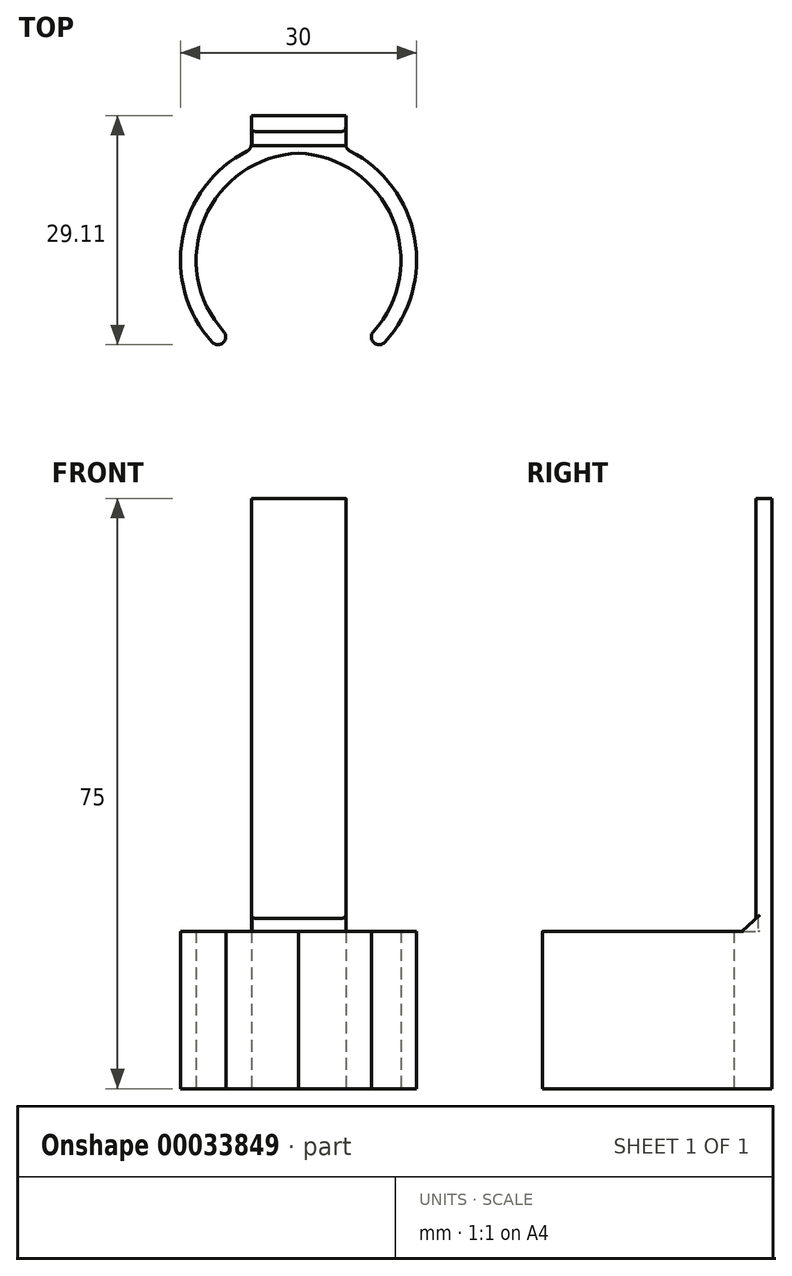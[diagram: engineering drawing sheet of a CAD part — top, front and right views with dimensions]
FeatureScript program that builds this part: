
annotation { "Feature Type Name" : "Feature", "Feature Type Description" : "" }
export const myFeature = defineFeature(function(context is Context, id is Id, definition is map)
    precondition{}
    {
        {
            var Q0;
            Q0=qCreatedBy(makeId("Top.planeOp"),FACE);
            var sketch = newSketch(context, id + "F0", { "sketchPlane" : qUnion([Q0])});
            skCircle(sketch, "E0", {"center": v(0, 0) * mm, "radius": 14.5 * mm, "construction": true});
            skCircle(sketch, "E1", {"center": v(0, 0) * mm, "radius": 12.5 * mm, "construction": true});
            skLineSegment(sketch, "E2", {"start": v(0, 0) * mm, "end": v(10.25, -10.25) * mm, "construction": true});
            skArc(sketch, "E3", {"start": v(9.5, -8.16) * mm, "mid": v(11.95, 6.19) * mm, "end": v(0, 14.5) * mm});
            skArc(sketch, "E4.0", {"start": v(10.98, -9.5) * mm, "mid": v(14.75, 3.74) * mm, "end": v(6.54, 14.8) * mm});
            skLineSegment(sketch, "E5", {"start": v(9.53, -9.53) * mm, "end": v(9.53, -9.53) * mm});
            skPoint(sketch, "E6.visualSharp", {"position": v(8.84, -8.84) * mm});
            skArc(sketch, "E6.filletArc", {"start": v(9.5, -8.16) * mm, "mid": v(9.24, -8.85) * mm, "end": v(9.53, -9.53) * mm});
            skPoint(sketch, "E7.visualSharp", {"position": v(10.25, -10.25) * mm});
            skArc(sketch, "E7.filletArc", {"start": v(9.53, -9.53) * mm, "mid": v(10.27, -9.83) * mm, "end": v(10.98, -9.5) * mm});
            skArc(sketch, "E8.MirrorCS", {"start": v(-10.98, -9.5) * mm, "mid": v(-14.75, 3.74) * mm, "end": v(-6.54, 14.8) * mm});
            skArc(sketch, "E9.MirrorCS", {"start": v(-9.5, -8.16) * mm, "mid": v(-11.95, 6.19) * mm, "end": v(0, 14.5) * mm});
            skArc(sketch, "E10.MirrorCS", {"start": v(-9.5, -8.16) * mm, "mid": v(-9.24, -8.85) * mm, "end": v(-9.53, -9.53) * mm});
            skArc(sketch, "E11.MirrorCS", {"start": v(-9.53, -9.53) * mm, "mid": v(-10.27, -9.83) * mm, "end": v(-10.98, -9.5) * mm});
            skLineSegment(sketch, "E12", {"start": v(6, 15.68) * mm, "end": v(6, 17.28) * mm});
            skLineSegment(sketch, "E13", {"start": v(6, 17.28) * mm, "end": v(0, 17.28) * mm});
            skPoint(sketch, "E14.start.orphan", {"position": v(0, 15.62) * mm});
            skLineSegment(sketch, "E15.MirrorCS", {"start": v(-6, 17.28) * mm, "end": v(0, 17.28) * mm});
            skLineSegment(sketch, "E16.MirrorCS", {"start": v(-6, 15.68) * mm, "end": v(-6, 17.28) * mm});
            skPoint(sketch, "E17.end.orphan", {"position": v(0.08, 16.5) * mm});
            skPoint(sketch, "E17.start.orphan", {"position": v(-0.08, 16.5) * mm});
            skPoint(sketch, "E18.visualSharp", {"position": v(-6, 15.06) * mm});
            skArc(sketch, "E18.filletArc", {"start": v(-6.54, 14.8) * mm, "mid": v(-6.15, 15.16) * mm, "end": v(-6, 15.68) * mm});
            skPoint(sketch, "E19.visualSharp", {"position": v(6, 15.06) * mm});
            skArc(sketch, "E19.filletArc", {"start": v(6, 15.68) * mm, "mid": v(6.15, 15.16) * mm, "end": v(6.54, 14.8) * mm});
            skSolve(sketch);
        }
        {
            var Q0;
            Q0=qSketchRegion(id+"F0",true);
            extrude(context, id + "F1", {"entities" : qUnion([Q0]), "depth" : 20 * mm});
        }
        {
            var Q0;
            Q0=makeQuery(id+"F1.opExtrude","CAP_FACE",FACE,{"disambiguationData":[OSD([sQuery(id+"F0.wireOp",EDGE,"E3"),sQuery(id+"F0.wireOp",EDGE,"E4.0"),sQuery(id+"F0.wireOp",EDGE,"E6.filletArc"),sQuery(id+"F0.wireOp",EDGE,"E7.filletArc"),sQuery(id+"F0.wireOp",EDGE,"E8.MirrorCS"),sQuery(id+"F0.wireOp",EDGE,"E9.MirrorCS"),sQuery(id+"F0.wireOp",EDGE,"E10.MirrorCS"),sQuery(id+"F0.wireOp",EDGE,"E11.MirrorCS"),sQuery(id+"F0.wireOp",EDGE,"E12"),sQuery(id+"F0.wireOp",EDGE,"E13"),sQuery(id+"F0.wireOp",EDGE,"E15.MirrorCS"),sQuery(id+"F0.wireOp",EDGE,"E16.MirrorCS"),sQuery(id+"F0.wireOp",EDGE,"E18.filletArc"),sQuery(id+"F0.wireOp",EDGE,"E19.filletArc")])],"isStart":true});
            var sketch = newSketch(context, id + "F2", { "sketchPlane" : qUnion([Q0])});
            skLineSegment(sketch, "E20.bottom", {"start": v(6, -17.28) * mm, "end": v(-6, -17.28) * mm});
            skLineSegment(sketch, "E20.top", {"start": v(6, -19.28) * mm, "end": v(-6, -19.28) * mm});
            skLineSegment(sketch, "E20.left", {"start": v(6, -17.28) * mm, "end": v(6, -19.28) * mm});
            skLineSegment(sketch, "E20.right", {"start": v(-6, -17.28) * mm, "end": v(-6, -19.28) * mm});
            skSolve(sketch);
        }
        {
            var Q0;
            Q0=qSketchRegion(id+"F2",true);
            extrude(context, id + "F3", {"entities" : qUnion([Q0]), "oppositeDirection" : true, "depth" : 75 * mm});
        }
        {
            var Q0;
            Q0=makeQuery(id+"F3.opExtrude","SWEPT_FACE",FACE,{"disambiguationData":[OSD([sQuery(id+"F2.wireOp",EDGE,"E20.left")])]});
            var sketch = newSketch(context, id + "F4", { "sketchPlane" : qUnion([Q0])});
            skLineSegment(sketch, "E21", {"start": v(14.9, 19.5) * mm, "end": v(17.28, 19.5) * mm});
            skLineSegment(sketch, "E22", {"start": v(17.28, 19.5) * mm, "end": v(17.28, 21.65) * mm});
            skLineSegment(sketch, "E23", {"start": v(17.28, 21.65) * mm, "end": v(14.9, 19.5) * mm});
            skSolve(sketch);
        }
        {
            var Q0;
            Q0=qSketchRegion(id+"F4",true);
            extrude(context, id + "F5", {"entities" : qUnion([Q0]), "operationType" : NewBodyOperationType.ADD, "oppositeDirection" : true, "depth" : 11.93 * mm});
        }
        {
            var Q0;
            {var subQ0=sQuery(id+"F2.wireOp",EDGE,"E20.bottom");var subQ1=sQuery(id+"F2.wireOp",EDGE,"E20.left");var subQ2=sQuery(id+"F4.wireOp",EDGE,"E23");Q0=makeQuery(id+"F5.boolean.opBoolean","SPLIT",EDGE,{"disambiguationData":[TD([makeQuery(id+"F5.opExtrude","SWEPT_FACE",FACE,{"disambiguationData":[OSD([subQ2])]})])],"derivedFrom":makeQuery(id+"F3.opExtrude","SWEPT_EDGE",EDGE,{"disambiguationData":[OSD([sQuery(id+"F0.wireOp",EDGE,"E12"),subQ0,subQ1])]})});}
            var Q1;
            Q1=makeQuery(id+"F3.opExtrude","SWEPT_EDGE",EDGE,{"disambiguationData":[OSD([sQuery(id+"F0.wireOp",EDGE,"E16.MirrorCS"),sQuery(id+"F2.wireOp",EDGE,"E20.bottom"),sQuery(id+"F2.wireOp",EDGE,"E20.right")])]});
            fillet(context, id + "F6", {"entities" : qUnion([Q0, Q1]), "radius" : .5 * mm, "tangentPropagation" : true, "allowEdgeOverflow" : false});
        }
    });
